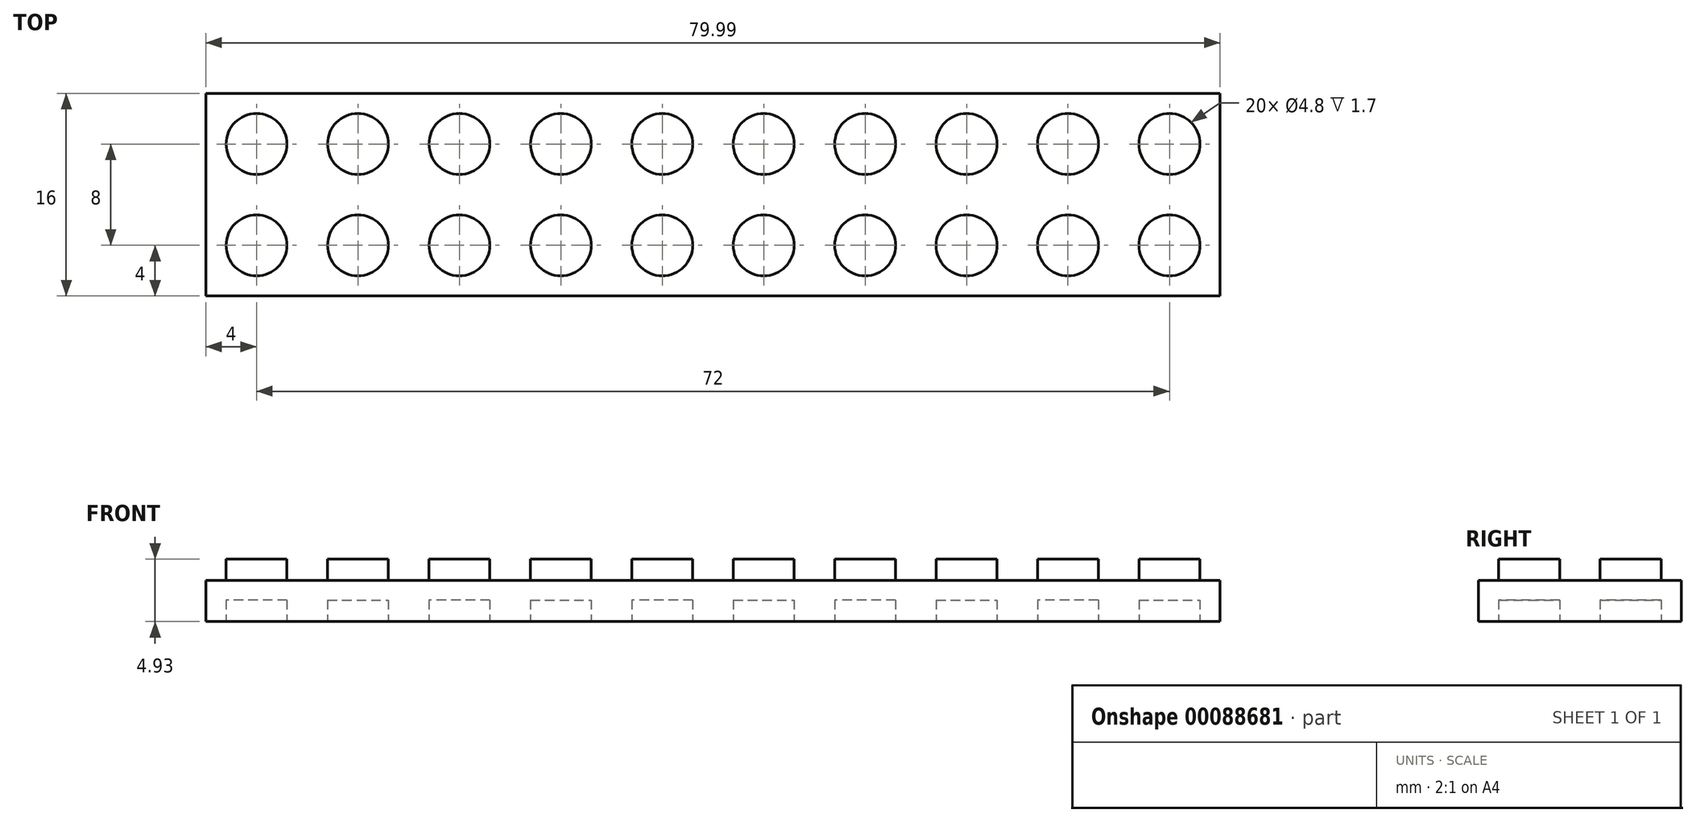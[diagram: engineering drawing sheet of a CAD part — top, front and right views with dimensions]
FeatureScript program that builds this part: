
annotation { "Feature Type Name" : "Feature", "Feature Type Description" : "" }
export const myFeature = defineFeature(function(context is Context, id is Id, definition is map)
    precondition{}
    {
        {
            var Q0;
            Q0=qCreatedBy(makeId("Front.planeOp"),FACE);
            var sketch = newSketch(context, id + "F0", { "sketchPlane" : qUnion([Q0])});
            skLineSegment(sketch, "E0.bottom", {"start": v(-4, 3.23) * mm, "end": v(-2.4, 3.23) * mm});
            skLineSegment(sketch, "E0.top", {"start": v(-4, 0) * mm, "end": v(4, 0) * mm});
            skLineSegment(sketch, "E0.left", {"start": v(-4, 3.23) * mm, "end": v(-4, 0) * mm});
            skLineSegment(sketch, "E0.right", {"start": v(4, 3.23) * mm, "end": v(4, 0) * mm});
            skLineSegment(sketch, "E1.top", {"start": v(-2.4, 4.93) * mm, "end": v(2.4, 4.93) * mm});
            skLineSegment(sketch, "E1.left", {"start": v(-2.4, 3.23) * mm, "end": v(-2.4, 4.93) * mm});
            skLineSegment(sketch, "E1.right", {"start": v(2.4, 3.23) * mm, "end": v(2.4, 4.93) * mm});
            skLineSegment(sketch, "E2", {"start": v(0, 0) * mm, "end": v(0, 24.04) * mm, "construction": true});
            skLineSegment(sketch, "E3.trimOffspring", {"start": v(2.4, 3.23) * mm, "end": v(4, 3.23) * mm});
            skSolve(sketch);
        }
        {
            var Q0;
            Q0=makeQuery(id+"F0.imprint","IMPRINT",FACE,{"disambiguationData":[TD([[makeQuery(id+"F0.imprint","IMPRINT",EDGE,{"derivedFrom":sQuery(id+"F0.wireOp",EDGE,"E0.bottom")}),-1.0]])]});
            extrude(context, id + "F1", {"entities" : qUnion([Q0]), "depth" : 8 * mm});
        }
        {
            var Q0;
            Q0=qCreatedBy(makeId("Top.planeOp"),FACE);
            var Q1;
            Q1=makeQuery(id+"F1.opExtrude","CAP_VERTEX",VERTEX,{"disambiguationData":[OSD([sQuery(id+"F0.wireOp",EDGE,"E1.top"),sQuery(id+"F0.wireOp",EDGE,"E1.right")])],"isStart":true});
            cPlane(context, id + "F2", {"entities" : qUnion([Q0, Q1]), "cplaneType" : CPlaneType.PLANE_POINT, "offset" : 152.4 * mm, "width" : 152.4 * mm, "height" : 152.4 * mm});
        }
        {
            var Q0;
            Q0=qCreatedBy(id+"F2.planeOp",FACE);
            var sketch = newSketch(context, id + "F3", { "sketchPlane" : qUnion([Q0])});
            skLineSegment(sketch, "E4.0", {"start": v(-4, -8) * mm, "end": v(-4, 0) * mm});
            skLineSegment(sketch, "E5.0", {"start": v(4, -8) * mm, "end": v(4, 0) * mm});
            skLineSegment(sketch, "E6", {"start": v(-4, 0) * mm, "end": v(4, 0) * mm});
            skLineSegment(sketch, "E7", {"start": v(-4, -8) * mm, "end": v(4, -8) * mm});
            skLineSegment(sketch, "E8", {"start": v(-4, 0) * mm, "end": v(4, -8) * mm, "construction": true});
            skLineSegment(sketch, "E9", {"start": v(-4, -8) * mm, "end": v(4, 0) * mm, "construction": true});
            skCircle(sketch, "E10", {"center": v(0, -4) * mm, "radius": 2.4 * mm});
            skSolve(sketch);
        }
        {
            var Q0;
            Q0=qSketchRegion(id+"F3",true);
            var Q1;
            Q1=makeQuery(id+"F1.opExtrude","SWEPT_FACE",FACE,{"disambiguationData":[OSD([sQuery(id+"F0.wireOp",EDGE,"E0.bottom")])]});
            extrude(context, id + "F4", {"entities" : qUnion([Q0]), "operationType" : NewBodyOperationType.REMOVE, "endBound" : BoundingType.UP_TO_SURFACE, "oppositeDirection" : true, "endBoundEntityFace" : qUnion([Q1]), "depth" : 25.4 * mm});
        }
        {
            var Q0;
            Q0=qCreatedBy(makeId("Top.planeOp"),FACE);
            var sketch = newSketch(context, id + "F5", { "sketchPlane" : qUnion([Q0])});
            skCircle(sketch, "E11.0", {"center": v(0, -4) * mm, "radius": 2.4 * mm});
            skSolve(sketch);
        }
        {
            var Q0;
            Q0=makeQuery(id+"F5.imprint","IMPRINT",FACE,{"disambiguationData":[TD([[makeQuery(id+"F5.imprint","IMPRINT",EDGE,{"derivedFrom":sQuery(id+"F5.wireOp",EDGE,"E11.0")}),1.0]])]});
            extrude(context, id + "F6", {"entities" : qUnion([Q0]), "operationType" : NewBodyOperationType.REMOVE, "depth" : 1.7 * mm});
        }
        {
            var Q0;
            Q0=qCreatedBy(makeId("Right.planeOp"),FACE);
            var Q1;
            Q1=makeQuery(id+"F1.opExtrude","CAP_VERTEX",VERTEX,{"disambiguationData":[OSD([sQuery(id+"F0.wireOp",EDGE,"E0.right"),sQuery(id+"F0.wireOp",EDGE,"E3.trimOffspring")])],"isStart":false});
            cPlane(context, id + "F7", {"entities" : qUnion([Q0, Q1]), "cplaneType" : CPlaneType.PLANE_POINT, "offset" : 152.4 * mm, "width" : 152.4 * mm, "height" : 152.4 * mm});
        }
        {
            var Q0;
            Q0=makeQuery(id+"F1.opExtrude","SWEPT_BODY",BODY,{"disambiguationData":[OSD([sQuery(id+"F0.wireOp",EDGE,"E0.bottom"),sQuery(id+"F0.wireOp",EDGE,"E0.top"),sQuery(id+"F0.wireOp",EDGE,"E0.left"),sQuery(id+"F0.wireOp",EDGE,"E0.right"),sQuery(id+"F0.wireOp",EDGE,"E1.top"),sQuery(id+"F0.wireOp",EDGE,"E1.left"),sQuery(id+"F0.wireOp",EDGE,"E1.right"),sQuery(id+"F0.wireOp",EDGE,"E3.trimOffspring")])]});
            var Q1;
            Q1=qCreatedBy(id+"F7.planeOp",FACE);
            mirror(context, id + "F8", {"operationType" : NewBodyOperationType.ADD, "entities" : qUnion([Q0]), "mirrorPlane" : qUnion([Q1])});
        }
        {
            var Q0;
            Q0=makeQuery(id+"F1.opExtrude","SWEPT_BODY",BODY,{"disambiguationData":[OSD([sQuery(id+"F0.wireOp",EDGE,"E0.bottom"),sQuery(id+"F0.wireOp",EDGE,"E0.top"),sQuery(id+"F0.wireOp",EDGE,"E0.left"),sQuery(id+"F0.wireOp",EDGE,"E0.right"),sQuery(id+"F0.wireOp",EDGE,"E1.top"),sQuery(id+"F0.wireOp",EDGE,"E1.left"),sQuery(id+"F0.wireOp",EDGE,"E1.right"),sQuery(id+"F0.wireOp",EDGE,"E3.trimOffspring")])]});
            var Q1;
            Q1=qCreatedBy(makeId("Front.planeOp"),FACE);
            mirror(context, id + "F9", {"operationType" : NewBodyOperationType.ADD, "entities" : qUnion([Q0]), "mirrorPlane" : qUnion([Q1])});
        }
        {
            var Q0;
            Q0=qCreatedBy(id+"F7.planeOp",FACE);
            var Q1;
            Q1=makeQuery(id+"F9.opPattern","COPY",VERTEX,{"derivedFrom":makeQuery(id+"F8.opPattern","COPY",VERTEX,{"derivedFrom":makeQuery(id+"F1.opExtrude","CAP_VERTEX",VERTEX,{"disambiguationData":[OSD([sQuery(id+"F0.wireOp",EDGE,"E0.bottom"),sQuery(id+"F0.wireOp",EDGE,"E0.left")])],"isStart":false}),"instanceName":"1"}),"instanceName":"1"});
            cPlane(context, id + "F10", {"entities" : qUnion([Q0, Q1]), "cplaneType" : CPlaneType.PLANE_POINT, "offset" : 152.4 * mm, "width" : 152.4 * mm, "height" : 152.4 * mm});
        }
        {
            var Q0;
            Q0=makeQuery(id+"F1.opExtrude","SWEPT_BODY",BODY,{"disambiguationData":[OSD([sQuery(id+"F0.wireOp",EDGE,"E0.bottom"),sQuery(id+"F0.wireOp",EDGE,"E0.top"),sQuery(id+"F0.wireOp",EDGE,"E0.left"),sQuery(id+"F0.wireOp",EDGE,"E0.right"),sQuery(id+"F0.wireOp",EDGE,"E1.top"),sQuery(id+"F0.wireOp",EDGE,"E1.left"),sQuery(id+"F0.wireOp",EDGE,"E1.right"),sQuery(id+"F0.wireOp",EDGE,"E3.trimOffspring")])]});
            var Q1;
            Q1=qCreatedBy(id+"F10.planeOp",FACE);
            mirror(context, id + "F11", {"operationType" : NewBodyOperationType.ADD, "entities" : qUnion([Q0]), "mirrorPlane" : qUnion([Q1])});
        }
        {
            var Q0;
            Q0=makeQuery(id+"F1.opExtrude","SWEPT_BODY",BODY,{"disambiguationData":[OSD([sQuery(id+"F0.wireOp",EDGE,"E0.bottom"),sQuery(id+"F0.wireOp",EDGE,"E0.top"),sQuery(id+"F0.wireOp",EDGE,"E0.left"),sQuery(id+"F0.wireOp",EDGE,"E0.right"),sQuery(id+"F0.wireOp",EDGE,"E1.top"),sQuery(id+"F0.wireOp",EDGE,"E1.left"),sQuery(id+"F0.wireOp",EDGE,"E1.right"),sQuery(id+"F0.wireOp",EDGE,"E3.trimOffspring")])]});
            var Q1;
            {var subQ0=makeQuery(id+"F1.opExtrude","SWEPT_FACE",FACE,{"disambiguationData":[OSD([sQuery(id+"F0.wireOp",EDGE,"E0.left")])]});Q1=makeQuery(id+"F11.opPattern","COPY",FACE,{"derivedFrom":makeQuery(id+"F9.boolean.opBoolean","MERGE",FACE,{"derivedFrom":[subQ0,makeQuery(id+"F9.opPattern","COPY",FACE,{"derivedFrom":subQ0,"instanceName":"1"})]}),"instanceName":"1"});}
            mirror(context, id + "F12", {"operationType" : NewBodyOperationType.ADD, "entities" : qUnion([Q0]), "mirrorPlane" : qUnion([Q1])});
        }
        {
            var Q0;
            Q0=makeQuery(id+"F1.opExtrude","SWEPT_BODY",BODY,{"disambiguationData":[OSD([sQuery(id+"F0.wireOp",EDGE,"E0.bottom"),sQuery(id+"F0.wireOp",EDGE,"E0.top"),sQuery(id+"F0.wireOp",EDGE,"E0.left"),sQuery(id+"F0.wireOp",EDGE,"E0.right"),sQuery(id+"F0.wireOp",EDGE,"E1.top"),sQuery(id+"F0.wireOp",EDGE,"E1.left"),sQuery(id+"F0.wireOp",EDGE,"E1.right"),sQuery(id+"F0.wireOp",EDGE,"E3.trimOffspring")])]});
            var Q1;
            {var subQ0=makeQuery(id+"F1.opExtrude","SWEPT_FACE",FACE,{"disambiguationData":[OSD([sQuery(id+"F0.wireOp",EDGE,"E0.left")])]});Q1=makeQuery(id+"F12.opPattern","COPY",FACE,{"derivedFrom":makeQuery(id+"F9.boolean.opBoolean","MERGE",FACE,{"derivedFrom":[subQ0,makeQuery(id+"F9.opPattern","COPY",FACE,{"derivedFrom":subQ0,"instanceName":"1"})]}),"instanceName":"1"});}
            mirror(context, id + "F13", {"operationType" : NewBodyOperationType.ADD, "entities" : qUnion([Q0]), "mirrorPlane" : qUnion([Q1])});
        }
        {
            var Q0;
            {var subQ0=makeQuery(id+"F1.opExtrude","SWEPT_FACE",FACE,{"disambiguationData":[OSD([sQuery(id+"F0.wireOp",EDGE,"E0.left")])]});Q0=makeQuery(id+"F13.opPattern","COPY",FACE,{"derivedFrom":makeQuery(id+"F9.boolean.opBoolean","MERGE",FACE,{"derivedFrom":[subQ0,makeQuery(id+"F9.opPattern","COPY",FACE,{"derivedFrom":subQ0,"instanceName":"1"})]}),"instanceName":"1"});}
            var sketch = newSketch(context, id + "F14", { "sketchPlane" : qUnion([Q0])});
            skLineSegment(sketch, "E12.bottom", {"start": v(17.18, 7.61) * mm, "end": v(-8.16, 7.61) * mm});
            skLineSegment(sketch, "E12.top", {"start": v(17.18, -7.61) * mm, "end": v(-8.16, -7.61) * mm});
            skLineSegment(sketch, "E12.left", {"start": v(17.18, 7.61) * mm, "end": v(17.18, -7.61) * mm});
            skLineSegment(sketch, "E12.right", {"start": v(-8.16, 7.61) * mm, "end": v(-8.16, -7.61) * mm});
            skPoint(sketch, "E12.middle", {"position": v(4.51, 0) * mm});
            skSolve(sketch);
        }
        {
            var Q0;
            Q0 = qSketchRegion(id + "F14", true);
            extrude(context, id + "F15", {"entities" : qUnion([Q0]), "operationType" : NewBodyOperationType.REMOVE, "oppositeDirection" : true, "depth" : .315 * 152.4 * mm, "offsetDistance" : 25.4 * mm});
        }
    });
